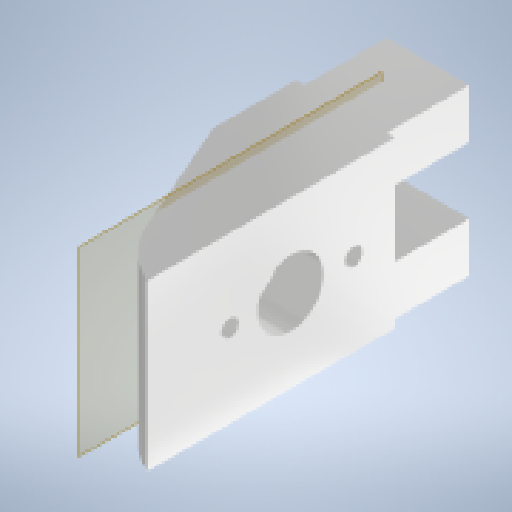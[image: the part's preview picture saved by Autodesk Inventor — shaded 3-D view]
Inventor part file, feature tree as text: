
AUTODESK INVENTOR PART (.ipt)
format: ipt  version: 2025 (Build 290162010, 162A)  size: 216,576 bytes
history: native  units: mm
features: sketch x6, other x4, extrude x3, hole x3, reference x2, plane x1
ambient origin geometry x8: Origin, YZ Plane, XZ Plane, XY Plane, X Axis, Y Axis, Z Axis, Center Point
bodies: Volumenkörper1 (feature_tree)
feature tree (19):
  extrude  "Extrusion1"  Depth=30.0mm TaperAngle=0.0deg
  hole  "Bohrung2"  [1 undecoded]
  sketch  "Skizze6"  dims[d16=1.567mm d17=8.0mm d18=4.0mm d19=2.0mm d20=90.0deg d21=10.0mm d22=20.594885mm d30=-10.0mm]
  plane  "Arbeitsebene1"
  hole  "Bohrung4"  [1 undecoded]
  extrude  "Extrusion2"  Depth=15.0mm
  hole  "Bohrung5"  [1 undecoded]
  extrude  "Extrusion3"  Depth=14.0mm
  sketch  "Skizze1"  dims[d0=5.0mm d1=45.0mm d2=30.0mm d3=0.0mm]
  reference  "Referenz1"
  sketch  "Skizze3"  dims[d4=15.0mm d14=6.5mm]
  reference  "Referenz3"
  sketch  "Skizze5"  dims[d15=5.0mm]
  sketch  "Skizze7"  dims[d31=15.0mm d32=15.0mm]
  sketch  "Skizze8"  dims[d33=3.2mm d34=6.0mm d35=6.3mm d36=2.0mm d37=90.0deg d38=8.0mm d39=20.594885mm d40=12.0mm d41=14.0mm d42=0.0mm d43=0.0mm d44=3.2mm d45=6.0mm d46=6.3mm d47=2.0mm d48=90.0deg d49=8.0mm d50=20.594885mm d51=12.0mm d52=8.0mm d53=0.0mm]
  other  "<userpath>\GIT\HDVKBM\CAD\Krandemonstrator\Demonstrator.iam"
  other  "Demonstrator.iam"
  other  "Träger:1"
  other  "AS 1112 (2) - Metrisch M4  Typ 5:1"
note: 3 required parameter values undecoded (feature->parameter linkage not recoverable at this tier; creation-order binding heuristic only, values carry confidence <= 0.55)
